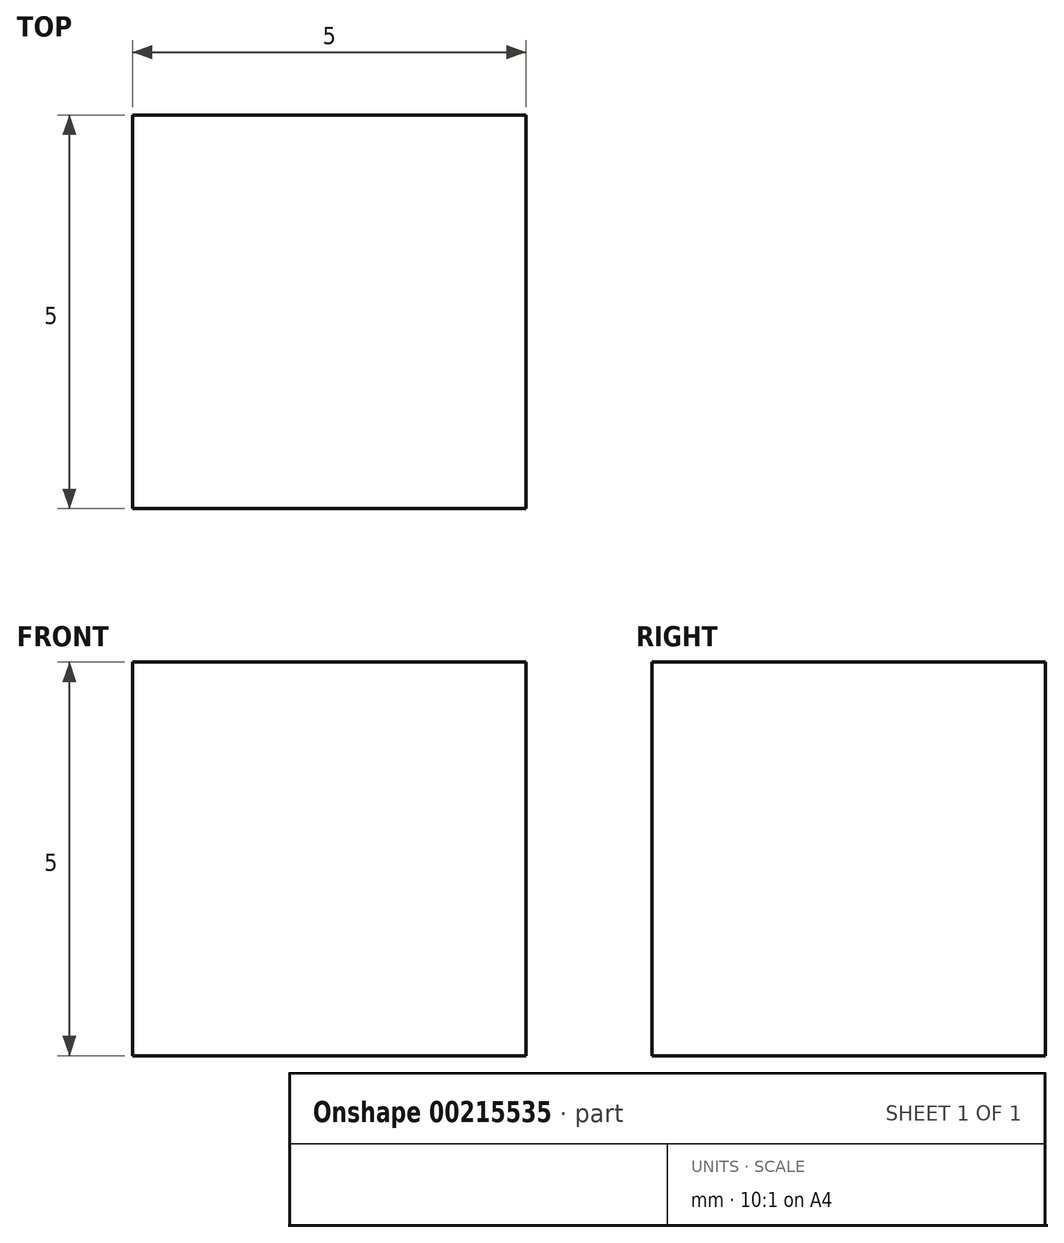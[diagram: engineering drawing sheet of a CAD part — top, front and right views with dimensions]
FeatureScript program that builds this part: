
annotation { "Feature Type Name" : "Feature", "Feature Type Description" : "" }
export const myFeature = defineFeature(function(context is Context, id is Id, definition is map)
    precondition{}
    {
        {
            var Q0;
            Q0=qCreatedBy(makeId("Front.planeOp"),FACE);
            var sketch = newSketch(context, id + "F0", { "sketchPlane" : qUnion([Q0])});
            skLineSegment(sketch, "E0.bottom", {"start": v(2.5, -2.5) * mm, "end": v(-2.5, -2.5) * mm});
            skLineSegment(sketch, "E0.top", {"start": v(2.5, 2.5) * mm, "end": v(-2.5, 2.5) * mm});
            skLineSegment(sketch, "E0.left", {"start": v(2.5, -2.5) * mm, "end": v(2.5, 2.5) * mm});
            skLineSegment(sketch, "E0.right", {"start": v(-2.5, -2.5) * mm, "end": v(-2.5, 2.5) * mm});
            skPoint(sketch, "E0.middle", {"position": v(0, 0) * mm});
            skSolve(sketch);
        }
        {
            var Q0;
            Q0=makeQuery(id+"F0.imprint","IMPRINT",FACE,{"disambiguationData":[TD([[makeQuery(id+"F0.imprint","IMPRINT",EDGE,{"derivedFrom":sQuery(id+"F0.wireOp",EDGE,"E0.bottom")}),-1.0]])]});
            extrude(context, id + "F1", {"entities" : qUnion([Q0]), "depth" : 5 * mm});
        }
    });
